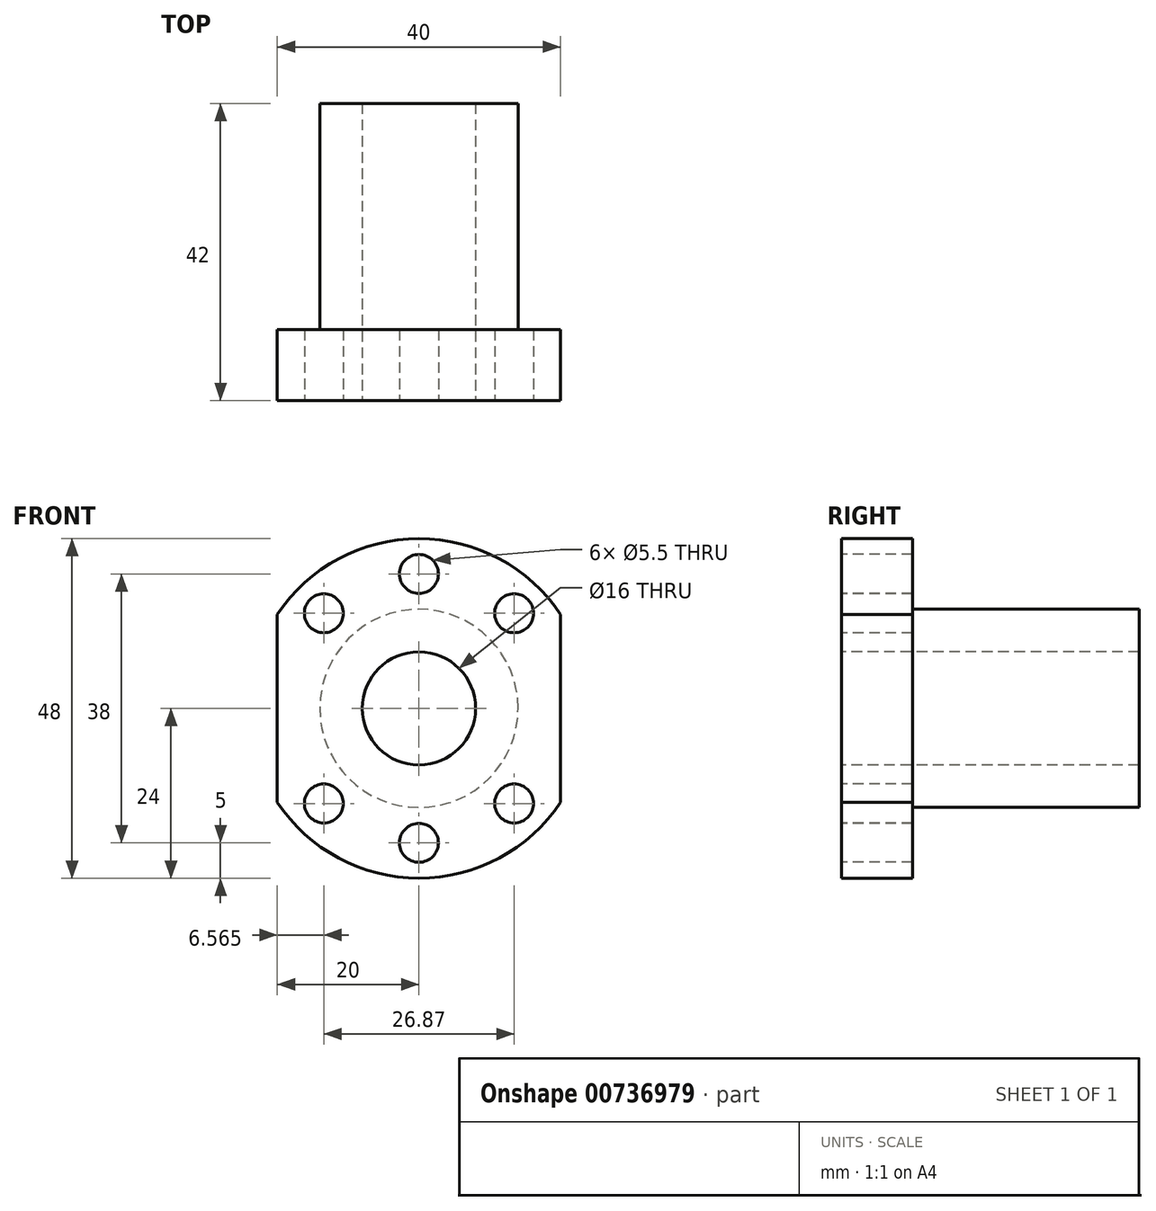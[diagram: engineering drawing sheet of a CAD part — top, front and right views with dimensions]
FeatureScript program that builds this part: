
annotation { "Feature Type Name" : "Feature", "Feature Type Description" : "" }
export const myFeature = defineFeature(function(context is Context, id is Id, definition is map)
    precondition{}
    {
        {
            var Q0;
            Q0=qCreatedBy(makeId("Front.planeOp"),FACE);
            var sketch = newSketch(context, id + "F0", { "sketchPlane" : qUnion([Q0])});
            skArc(sketch, "E0", {"start": v(-20, -13.27) * mm, "mid": v(0, -24) * mm, "end": v(20, -13.27) * mm});
            skLineSegment(sketch, "E1", {"start": v(-20, 13.27) * mm, "end": v(-20, -13.27) * mm});
            skLineSegment(sketch, "E2", {"start": v(0, 43.05) * mm, "end": v(0, -39.38) * mm, "construction": true});
            skLineSegment(sketch, "E3.MirrorCS", {"start": v(20, 13.27) * mm, "end": v(20, -13.27) * mm});
            skArc(sketch, "E4.trimOffspring", {"start": v(20, 13.27) * mm, "mid": v(0, 24) * mm, "end": v(-20, 13.27) * mm});
            skCircle(sketch, "E5", {"center": v(0, 0) * mm, "radius": 19 * mm, "construction": true});
            skCircle(sketch, "E6", {"center": v(0, 19) * mm, "radius": 2.75 * mm});
            skLineSegment(sketch, "E7", {"start": v(0, 0) * mm, "end": v(24.15, 24.15) * mm, "construction": true});
            skCircle(sketch, "E8", {"center": v(13.44, 13.44) * mm, "radius": 2.75 * mm});
            skCircle(sketch, "E9.MirrorC", {"center": v(-13.44, 13.44) * mm, "radius": 2.75 * mm});
            skCircle(sketch, "E10.MirrorC", {"center": v(-13.44, -13.44) * mm, "radius": 2.75 * mm});
            skCircle(sketch, "E11.MirrorC", {"center": v(0, -19) * mm, "radius": 2.75 * mm});
            skCircle(sketch, "E12.MirrorC", {"center": v(13.44, -13.44) * mm, "radius": 2.75 * mm});
            skCircle(sketch, "E13", {"center": v(0, 0) * mm, "radius": 8 * mm});
            skSolve(sketch);
        }
        {
            var Q0;
            Q0 = qSketchRegion(id + "F0", true);
            extrude(context, id + "F1", {"entities" : qUnion([Q0]), "oppositeDirection" : true, "depth" : 10 * mm, "offsetDistance" : 25 * mm});
        }
        {
            var Q0;
            Q0=makeQuery(id+"F1.opExtrude","CAP_FACE",FACE,{"disambiguationData":[OSD([sQuery(id+"F0.wireOp",EDGE,"E0"),sQuery(id+"F0.wireOp",EDGE,"E1"),sQuery(id+"F0.wireOp",EDGE,"E3.MirrorCS"),sQuery(id+"F0.wireOp",EDGE,"E4.trimOffspring"),sQuery(id+"F0.wireOp",EDGE,"E6"),sQuery(id+"F0.wireOp",EDGE,"E8"),sQuery(id+"F0.wireOp",EDGE,"E9.MirrorC"),sQuery(id+"F0.wireOp",EDGE,"E10.MirrorC"),sQuery(id+"F0.wireOp",EDGE,"E11.MirrorC"),sQuery(id+"F0.wireOp",EDGE,"E12.MirrorC")])],"isStart":false});
            var sketch = newSketch(context, id + "F2", { "sketchPlane" : qUnion([Q0])});
            skCircle(sketch, "E14", {"center": v(0, 0) * mm, "radius": 14 * mm});
            skSolve(sketch);
        }
        {
            var Q0;
            Q0=makeQuery(id+"F2.imprint","IMPRINT",FACE,{"disambiguationData":[TD([[makeQuery(id+"F2.imprint","IMPRINT",EDGE,{"derivedFrom":sQuery(id+"F2.wireOp",EDGE,"E14")}),1.0]])]});
            extrude(context, id + "F3", {"entities" : qUnion([Q0]), "operationType" : NewBodyOperationType.ADD, "depth" : 32 * mm, "offsetDistance" : 25 * mm});
        }
    });
